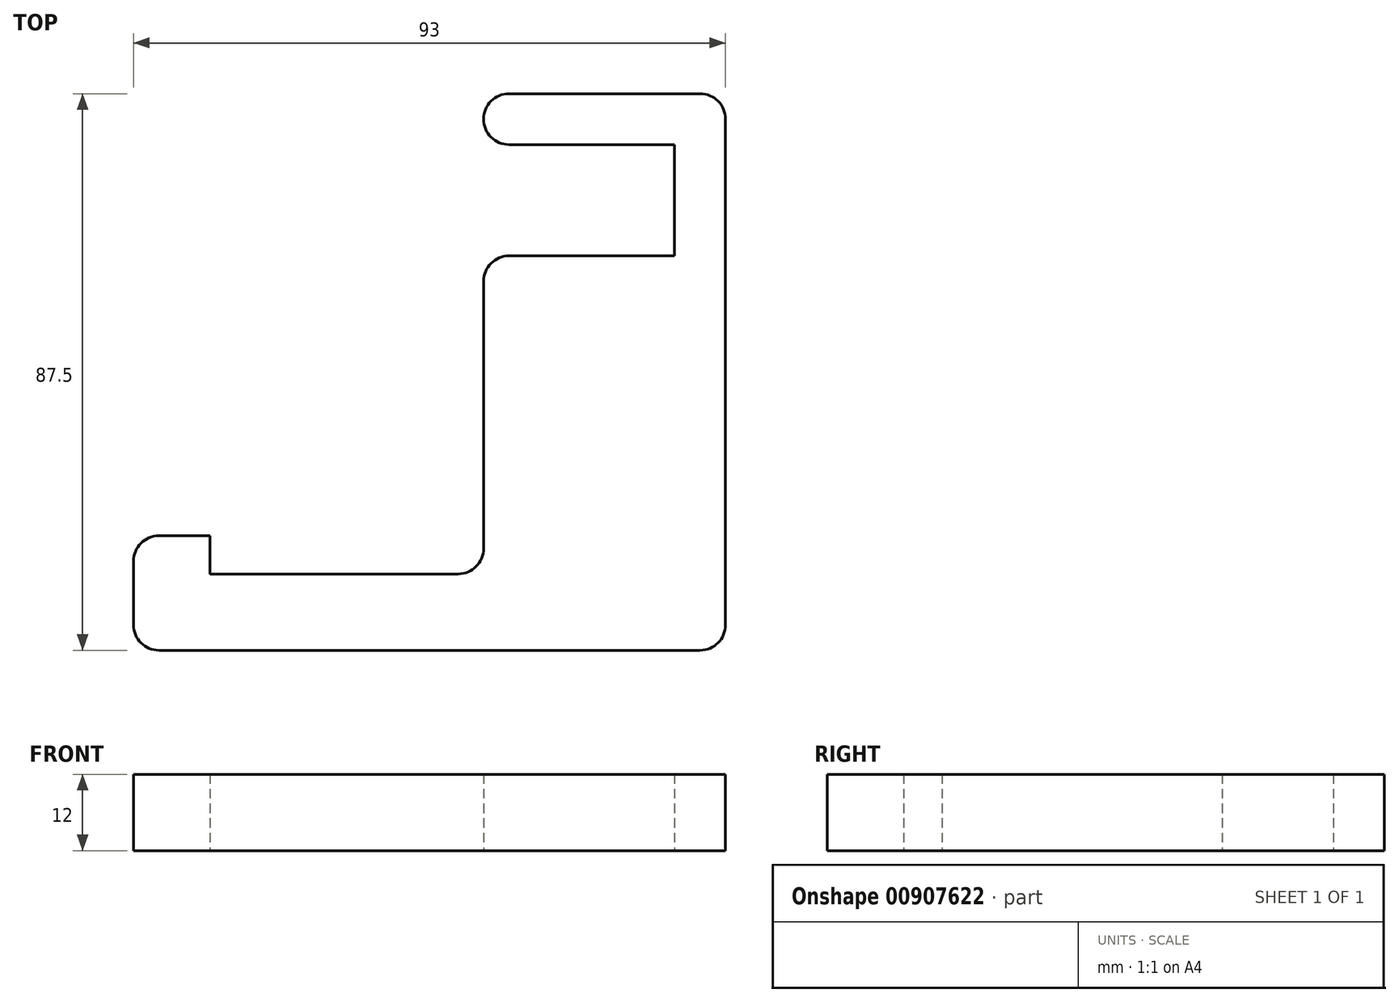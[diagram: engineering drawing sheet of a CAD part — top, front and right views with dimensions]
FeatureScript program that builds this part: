
annotation { "Feature Type Name" : "Feature", "Feature Type Description" : "" }
export const myFeature = defineFeature(function(context is Context, id is Id, definition is map)
    precondition{}
    {
        {
            var Q0;
            Q0=qCreatedBy(makeId("Top.planeOp"),FACE);
            var sketch = newSketch(context, id + "F0", { "sketchPlane" : qUnion([Q0])});
            skLineSegment(sketch, "E0", {"start": v(0, 0) * mm, "end": v(0, -8) * mm});
            skLineSegment(sketch, "E1", {"start": v(0, -8) * mm, "end": v(30, -8) * mm});
            skLineSegment(sketch, "E2", {"start": v(30, -8) * mm, "end": v(30, -25.5) * mm});
            skLineSegment(sketch, "E3", {"start": v(30, -25.5) * mm, "end": v(0, -25.5) * mm});
            skLineSegment(sketch, "E4", {"start": v(0, -25.5) * mm, "end": v(0, -75.5) * mm});
            skLineSegment(sketch, "E5", {"start": v(-55, -87.5) * mm, "end": v(38, -87.5) * mm});
            skLineSegment(sketch, "E6", {"start": v(38, -87.5) * mm, "end": v(38, 0) * mm});
            skLineSegment(sketch, "E7", {"start": v(38, 0) * mm, "end": v(0, 0) * mm});
            skLineSegment(sketch, "E8", {"start": v(-55, -69.5) * mm, "end": v(-43, -69.5) * mm});
            skLineSegment(sketch, "E9", {"start": v(-43, -69.5) * mm, "end": v(-43, -75.5) * mm});
            skLineSegment(sketch, "E10", {"start": v(-43, -75.5) * mm, "end": v(0, -75.5) * mm});
            skLineSegment(sketch, "E11", {"start": v(-55, -69.5) * mm, "end": v(-55, -87.5) * mm});
            skSolve(sketch);
        }
        {
            var Q0;
            Q0 = qSketchRegion(id + "F0", true);
            extrude(context, id + "F1", {"entities" : qUnion([Q0]), "depth" : 12 * mm, "offsetDistance" : 25 * mm});
        }
        {
            var Q0;
            Q0=makeQuery(id+"F1.opExtrude","SWEPT_EDGE",EDGE,{"disambiguationData":[OSD([sQuery(id+"F0.wireOp",EDGE,"E3"),sQuery(id+"F0.wireOp",EDGE,"E4")])]});
            var Q1;
            Q1=makeQuery(id+"F1.opExtrude","SWEPT_EDGE",EDGE,{"disambiguationData":[OSD([sQuery(id+"F0.wireOp",EDGE,"E0"),sQuery(id+"F0.wireOp",EDGE,"E1")])]});
            var Q2;
            Q2=makeQuery(id+"F1.opExtrude","SWEPT_EDGE",EDGE,{"disambiguationData":[OSD([sQuery(id+"F0.wireOp",EDGE,"E6"),sQuery(id+"F0.wireOp",EDGE,"E7")])]});
            var Q3;
            Q3=makeQuery(id+"F1.opExtrude","SWEPT_EDGE",EDGE,{"disambiguationData":[OSD([sQuery(id+"F0.wireOp",EDGE,"E5"),sQuery(id+"F0.wireOp",EDGE,"E6")])]});
            var Q4;
            Q4=makeQuery(id+"F1.opExtrude","SWEPT_EDGE",EDGE,{"disambiguationData":[OSD([sQuery(id+"F0.wireOp",EDGE,"E0"),sQuery(id+"F0.wireOp",EDGE,"E7")])]});
            var Q5;
            Q5=makeQuery(id+"F1.opExtrude","SWEPT_EDGE",EDGE,{"disambiguationData":[OSD([sQuery(id+"F0.wireOp",EDGE,"E4"),sQuery(id+"F0.wireOp",EDGE,"BmvVSOrI-arv2-eCNl-y9e8-13uhO79Pgq0i")])]});
            var Q6;
            Q6=makeQuery(id+"F1.opExtrude","SWEPT_EDGE",EDGE,{"disambiguationData":[OSD([sQuery(id+"F0.wireOp",EDGE,"BmvVSOrI-arv2-eCNl-y9e8-13uhO79Pgq0i"),sQuery(id+"F0.wireOp",EDGE,"Or619OzT-ieYu-aD12-7ilh-PgshZOE2rYor")])]});
            var Q7;
            Q7=makeQuery(id+"F1.opExtrude","SWEPT_EDGE",EDGE,{"disambiguationData":[OSD([sQuery(id+"F0.wireOp",EDGE,"Or619OzT-ieYu-aD12-7ilh-PgshZOE2rYor"),sQuery(id+"F0.wireOp",EDGE,"E5")])]});
            var Q8;
            Q8=makeQuery(id+"F1.opExtrude","SWEPT_EDGE",EDGE,{"disambiguationData":[OSD([sQuery(id+"F0.wireOp",EDGE,"E8"),sQuery(id+"F0.wireOp",EDGE,"E11")])]});
            fillet(context, id + "F2", {"entities" : qUnion([Q0, Q1, Q2, Q3, Q4, Q5, Q6, Q7, Q8]), "radius" : 4 * mm, "tangentPropagation" : true, "allowEdgeOverflow" : false});
        }
    });
